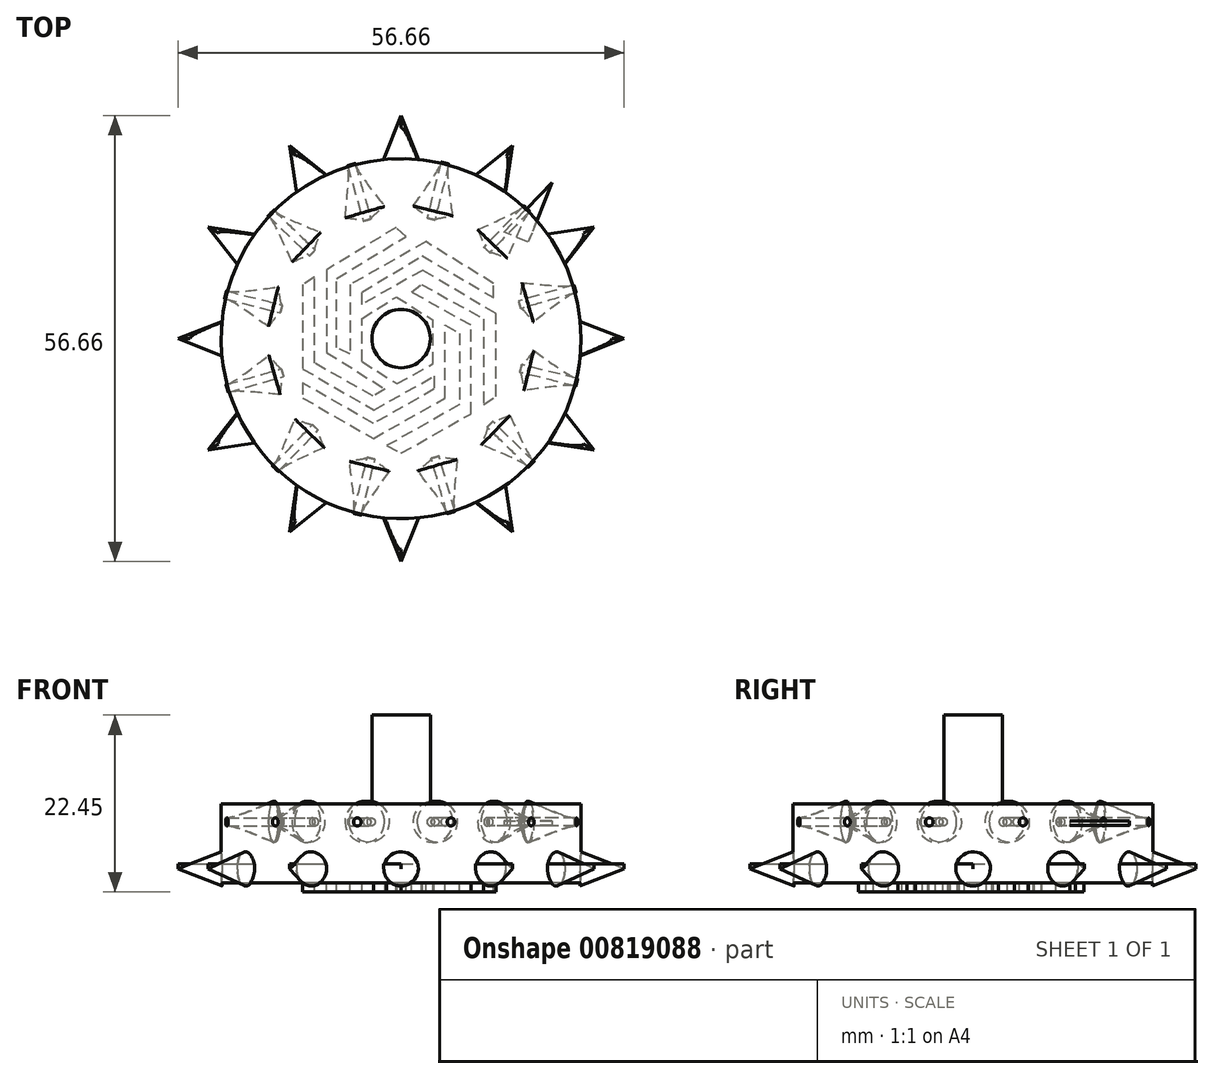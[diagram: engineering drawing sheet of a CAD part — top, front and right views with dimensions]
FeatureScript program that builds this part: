
annotation { "Feature Type Name" : "Feature", "Feature Type Description" : "" }
export const myFeature = defineFeature(function(context is Context, id is Id, definition is map)
    precondition{}
    {
        {
            var Q0;
            Q0=qCreatedBy(makeId("Top.planeOp"),FACE);
            var sketch = newSketch(context, id + "F0", { "sketchPlane" : qUnion([Q0])});
            skCircle(sketch, "E0", {"center": v(0, 0) * mm, "radius": 19.05 * mm});
            skSolve(sketch);
        }
        {
            var Q0;
            Q0=makeQuery(id+"F0.imprint","IMPRINT",FACE,{"disambiguationData":[TD([[makeQuery(id+"F0.imprint","IMPRINT",EDGE,{"derivedFrom":sQuery(id+"F0.wireOp",EDGE,"E0")}),1.0]])]});
            extrude(context, id + "F1", {"entities" : qUnion([Q0]), "depth" : 8.38 * mm, "offsetDistance" : 25.4 * mm});
        }
        {
            var Q0;
            Q0=makeQuery(id+"F1.opExtrude","CAP_FACE",FACE,{"disambiguationData":[OSD([sQuery(id+"F0.wireOp",EDGE,"E0")])],"isStart":false});
            var sketch = newSketch(context, id + "F2", { "sketchPlane" : qUnion([Q0])});
            skCircle(sketch, "E1", {"center": v(0, 0) * mm, "radius": 3.1 * mm});
            skSolve(sketch);
        }
        {
            var Q0;
            Q0=makeQuery(id+"F2.imprint","IMPRINT",FACE,{"disambiguationData":[TD([[makeQuery(id+"F2.imprint","IMPRINT",EDGE,{"derivedFrom":sQuery(id+"F2.wireOp",EDGE,"E1")}),1.0]])]});
            extrude(context, id + "F3", {"entities" : qUnion([Q0]), "operationType" : NewBodyOperationType.ADD, "depth" : 9.4 * mm, "offsetDistance" : 25.4 * mm});
        }
        {
            var Q0;
            Q0=qCreatedBy(makeId("Top.planeOp"),FACE);
            cPlane(context, id + "F4", {"entities" : qUnion([Q0]), "cplaneType" : CPlaneType.OFFSET, "offset" : 2.03 * mm, "width" : 152.4 * mm, "height" : 152.4 * mm});
        }
        {
            var Q0;
            Q0=qCreatedBy(id+"F4.planeOp",FACE);
            var sketch = newSketch(context, id + "F5", { "sketchPlane" : qUnion([Q0])});
            skLineSegment(sketch, "E2", {"start": v(0, 17.1) * mm, "end": v(0, 23.6) * mm});
            skLineSegment(sketch, "E3", {"start": v(0, 23.6) * mm, "end": v(2.57, 17.1) * mm});
            skLineSegment(sketch, "E4", {"start": v(0, 17.1) * mm, "end": v(2.57, 17.1) * mm});
            skSolve(sketch);
        }
        {
            var Q0;
            Q0=qSketchRegion(id+"F5",true);
            extrude(context, id + "F6", {"entities" : qUnion([Q0]), "operationType" : NewBodyOperationType.ADD, "oppositeDirection" : true, "depth" : 0.5 * mm, "offsetDistance" : 25.4 * mm});
        }
        {
            var Q0;
            Q0=makeQuery(id+"F6.opExtrude","CAP_FACE",FACE,{"disambiguationData":[OSD([sQuery(id+"F5.wireOp",EDGE,"E2"),sQuery(id+"F5.wireOp",EDGE,"E3"),sQuery(id+"F5.wireOp",EDGE,"E4")])],"isStart":false});
            var Q1;
            Q1=makeQuery(id+"F6.opExtrude","CAP_EDGE",EDGE,{"disambiguationData":[OSD([sQuery(id+"F5.wireOp",EDGE,"E2")])],"isStart":false});
            revolve(context, id + "F7", {"operationType" : NewBodyOperationType.ADD, "surfaceOperationType" : NewSurfaceOperationType.NEW, "entities" : qUnion([Q0]), "axis" : qUnion([Q1]), "revolveType" : RevolveType.FULL});
        }
        {
            var Q0;
            Q0=makeQuery(id+"F1.opExtrude","SWEPT_BODY",BODY,{"disambiguationData":[OSD([sQuery(id+"F0.wireOp",EDGE,"E0")])]});
            var Q1;
            Q1=makeQuery(id+"F3.opExtrude","CAP_EDGE",EDGE,{"disambiguationData":[OSD([sQuery(id+"F2.wireOp",EDGE,"E1")])],"isStart":false});
            circularPattern(context, id + "F8", {"entities" : qUnion([Q0]), "axis" : qUnion([Q1]), "angle" : 360 * degree, "instanceCount" : 12, "equalSpace" : true});
        }
        {
            var Q0;
            Q0=qCreatedBy(id+"F4.planeOp",FACE);
            cPlane(context, id + "F9", {"entities" : qUnion([Q0]), "cplaneType" : CPlaneType.OFFSET, "offset" : 4.06 * mm, "width" : 152.4 * mm, "height" : 152.4 * mm});
        }
        {
            var Q0;
            Q0=qCreatedBy(id+"F9.planeOp",FACE);
            var sketch = newSketch(context, id + "F10", { "sketchPlane" : qUnion([Q0])});
            skLineSegment(sketch, "E5", {"start": v(0, 0) * mm, "end": v(15.97, 16.54) * mm});
            skLineSegment(sketch, "E6", {"start": v(15.97, 16.54) * mm, "end": v(13.46, 10.25) * mm});
            skLineSegment(sketch, "E7", {"start": v(13.46, 10.25) * mm, "end": v(10.89, 11.27) * mm});
            skSolve(sketch);
        }
        {
            var Q0;
            Q0=qSketchRegion(id+"F10",true);
            extrude(context, id + "F11", {"entities" : qUnion([Q0]), "depth" : 0.5 * mm, "offsetDistance" : 25.4 * mm});
        }
        {
            var Q0;
            Q0=makeQuery(id+"F11.opExtrude","CAP_FACE",FACE,{"disambiguationData":[OSD([sQuery(id+"F10.wireOp",EDGE,"E5"),sQuery(id+"F10.wireOp",EDGE,"E6"),sQuery(id+"F10.wireOp",EDGE,"E7")])],"isStart":false});
            var Q1;
            Q1=makeQuery(id+"F11.opExtrude","CAP_EDGE",EDGE,{"disambiguationData":[OSD([sQuery(id+"F10.wireOp",EDGE,"E5")])],"isStart":true});
            revolve(context, id + "F12", {"surfaceOperationType" : NewSurfaceOperationType.NEW, "entities" : qUnion([Q0]), "axis" : qUnion([Q1]), "revolveType" : RevolveType.FULL});
        }
        {
            var Q0;
            Q0=makeQuery(id+"F12.opRevolve","SWEPT_BODY",BODY,{"disambiguationData":[OSD([sQuery(id+"F10.wireOp",EDGE,"E5"),sQuery(id+"F10.wireOp",EDGE,"E6"),sQuery(id+"F10.wireOp",EDGE,"E7")])]});
            var Q1;
            Q1=makeQuery(id+"F3.opExtrude","CAP_EDGE",EDGE,{"disambiguationData":[OSD([sQuery(id+"F2.wireOp",EDGE,"E1")])],"isStart":false});
            circularPattern(context, id + "F13", {"entities" : qUnion([Q0]), "axis" : qUnion([Q1]), "angle" : 360 * degree, "instanceCount" : 12, "equalSpace" : true});
        }
        {
            var Q0;
            Q0=makeQuery(id+"F8.opPattern","COPY",BODY,{"derivedFrom":makeQuery(id+"F1.opExtrude","SWEPT_BODY",BODY,{"disambiguationData":[OSD([sQuery(id+"F0.wireOp",EDGE,"E0")])]}),"instanceName":"6"});
            var Q1;
            Q1=makeQuery(id+"F8.opPattern","COPY",BODY,{"derivedFrom":makeQuery(id+"F1.opExtrude","SWEPT_BODY",BODY,{"disambiguationData":[OSD([sQuery(id+"F0.wireOp",EDGE,"E0")])]}),"instanceName":"5"});
            var Q2;
            Q2=makeQuery(id+"F8.opPattern","COPY",BODY,{"derivedFrom":makeQuery(id+"F1.opExtrude","SWEPT_BODY",BODY,{"disambiguationData":[OSD([sQuery(id+"F0.wireOp",EDGE,"E0")])]}),"instanceName":"3"});
            var Q3;
            Q3=makeQuery(id+"F1.opExtrude","SWEPT_BODY",BODY,{"disambiguationData":[OSD([sQuery(id+"F0.wireOp",EDGE,"E0")])]});
            var Q4;
            Q4=makeQuery(id+"F8.opPattern","COPY",BODY,{"derivedFrom":makeQuery(id+"F1.opExtrude","SWEPT_BODY",BODY,{"disambiguationData":[OSD([sQuery(id+"F0.wireOp",EDGE,"E0")])]}),"instanceName":"11"});
            var Q5;
            Q5=makeQuery(id+"F8.opPattern","COPY",BODY,{"derivedFrom":makeQuery(id+"F1.opExtrude","SWEPT_BODY",BODY,{"disambiguationData":[OSD([sQuery(id+"F0.wireOp",EDGE,"E0")])]}),"instanceName":"8"});
            var Q6;
            Q6=makeQuery(id+"F8.opPattern","COPY",BODY,{"derivedFrom":makeQuery(id+"F1.opExtrude","SWEPT_BODY",BODY,{"disambiguationData":[OSD([sQuery(id+"F0.wireOp",EDGE,"E0")])]}),"instanceName":"9"});
            var Q7;
            Q7=makeQuery(id+"F8.opPattern","COPY",BODY,{"derivedFrom":makeQuery(id+"F1.opExtrude","SWEPT_BODY",BODY,{"disambiguationData":[OSD([sQuery(id+"F0.wireOp",EDGE,"E0")])]}),"instanceName":"10"});
            var Q8;
            Q8=makeQuery(id+"F8.opPattern","COPY",BODY,{"derivedFrom":makeQuery(id+"F1.opExtrude","SWEPT_BODY",BODY,{"disambiguationData":[OSD([sQuery(id+"F0.wireOp",EDGE,"E0")])]}),"instanceName":"7"});
            var Q9;
            Q9=makeQuery(id+"F8.opPattern","COPY",BODY,{"derivedFrom":makeQuery(id+"F1.opExtrude","SWEPT_BODY",BODY,{"disambiguationData":[OSD([sQuery(id+"F0.wireOp",EDGE,"E0")])]}),"instanceName":"4"});
            var Q10;
            Q10=makeQuery(id+"F8.opPattern","COPY",BODY,{"derivedFrom":makeQuery(id+"F1.opExtrude","SWEPT_BODY",BODY,{"disambiguationData":[OSD([sQuery(id+"F0.wireOp",EDGE,"E0")])]}),"instanceName":"2"});
            var Q11;
            Q11=makeQuery(id+"F11.opExtrude","SWEPT_BODY",BODY,{"disambiguationData":[OSD([sQuery(id+"F10.wireOp",EDGE,"E5"),sQuery(id+"F10.wireOp",EDGE,"E6"),sQuery(id+"F10.wireOp",EDGE,"E7")])]});
            var Q12;
            Q12=makeQuery(id+"F8.opPattern","COPY",BODY,{"derivedFrom":makeQuery(id+"F1.opExtrude","SWEPT_BODY",BODY,{"disambiguationData":[OSD([sQuery(id+"F0.wireOp",EDGE,"E0")])]}),"instanceName":"1"});
            var Q13;
            Q13=sQuery(id+"F2.wireOp",VERTEX,"E1.center");
            transform(context, id + "F14", {"entities" : qUnion([Q0, Q1, Q2, Q3, Q4, Q5, Q6, Q7, Q8, Q9, Q10, Q11, Q12]), "transformType" : TransformType.SCALE_UNIFORMLY, "scale" : 1.2, "scalePoint" : qUnion([Q13]), "makeCopy" : false});
        }
        {
            var Q0;
            Q0=qCreatedBy(makeId("Top.planeOp"),FACE);
            var sketch = newSketch(context, id + "F15", { "sketchPlane" : qUnion([Q0])});
            skLineSegment(sketch, "E8", {"start": v(-12.5, 6.89) * mm, "end": v(-12.5, -3.83) * mm});
            skLineSegment(sketch, "E9", {"start": v(-12.5, -3.83) * mm, "end": v(-3.44, -9.07) * mm});
            skLineSegment(sketch, "E10", {"start": v(-3.44, -9.07) * mm, "end": v(4.2, -4.76) * mm});
            skLineSegment(sketch, "E11", {"start": v(4.2, -4.76) * mm, "end": v(4.2, -6.42) * mm});
            skLineSegment(sketch, "E12", {"start": v(4.2, -6.42) * mm, "end": v(-3.52, -10.78) * mm});
            skLineSegment(sketch, "E13", {"start": v(-3.52, -10.78) * mm, "end": v(-12.5, -5.62) * mm});
            skLineSegment(sketch, "E14", {"start": v(-12.5, -5.62) * mm, "end": v(-12.5, -7.53) * mm});
            skLineSegment(sketch, "E15", {"start": v(-12.5, -7.53) * mm, "end": v(-3.52, -12.69) * mm});
            skLineSegment(sketch, "E16", {"start": v(-3.52, -12.69) * mm, "end": v(5.6, -7.54) * mm});
            skLineSegment(sketch, "E17", {"start": v(5.6, -7.54) * mm, "end": v(5.6, 1.71) * mm});
            skLineSegment(sketch, "E18", {"start": v(5.6, 1.71) * mm, "end": v(7.4, 0.68) * mm});
            skLineSegment(sketch, "E19", {"start": v(7.4, 0.68) * mm, "end": v(7.4, -8.4) * mm});
            skLineSegment(sketch, "E20", {"start": v(7.4, -8.4) * mm, "end": v(-1.82, -13.6) * mm});
            skLineSegment(sketch, "E21", {"start": v(-1.82, -13.6) * mm, "end": v(0, -14.55) * mm});
            skLineSegment(sketch, "E22", {"start": v(0, -14.55) * mm, "end": v(8.86, -9.55) * mm});
            skLineSegment(sketch, "E23", {"start": v(8.86, -9.55) * mm, "end": v(8.86, 1.71) * mm});
            skLineSegment(sketch, "E24", {"start": v(8.86, 1.71) * mm, "end": v(1.3, 5.9) * mm});
            skLineSegment(sketch, "E25", {"start": v(1.3, 5.9) * mm, "end": v(2.6, 6.89) * mm});
            skLineSegment(sketch, "E26", {"start": v(2.6, 6.89) * mm, "end": v(10.49, 2.51) * mm});
            skLineSegment(sketch, "E27", {"start": v(10.49, 2.51) * mm, "end": v(10.49, -8.4) * mm});
            skLineSegment(sketch, "E28", {"start": v(10.49, -8.4) * mm, "end": v(12.03, -7.34) * mm});
            skLineSegment(sketch, "E29", {"start": v(12.03, -7.34) * mm, "end": v(12.03, 3.2) * mm});
            skLineSegment(sketch, "E30", {"start": v(12.03, 3.2) * mm, "end": v(2.72, 8.68) * mm});
            skLineSegment(sketch, "E31", {"start": v(2.72, 8.68) * mm, "end": v(-4.98, 4.36) * mm});
            skLineSegment(sketch, "E32", {"start": v(-4.98, 4.36) * mm, "end": v(-4.98, 5.9) * mm});
            skLineSegment(sketch, "E33", {"start": v(-4.98, 5.9) * mm, "end": v(2.66, 10.52) * mm});
            skLineSegment(sketch, "E34", {"start": v(2.66, 10.52) * mm, "end": v(11.72, 5.23) * mm});
            skLineSegment(sketch, "E35", {"start": v(11.72, 5.23) * mm, "end": v(11.72, 7.01) * mm});
            skLineSegment(sketch, "E36", {"start": v(11.72, 7.01) * mm, "end": v(3.15, 12.31) * mm});
            skLineSegment(sketch, "E37", {"start": v(3.15, 12.31) * mm, "end": v(-6.46, 6.89) * mm});
            skLineSegment(sketch, "E38", {"start": v(-6.46, 6.89) * mm, "end": v(-6.46, -1.98) * mm});
            skLineSegment(sketch, "E39", {"start": v(-6.46, -1.98) * mm, "end": v(-8.18, -1.12) * mm});
            skLineSegment(sketch, "E40", {"start": v(-8.18, -1.12) * mm, "end": v(-8.18, 7.63) * mm});
            skLineSegment(sketch, "E41", {"start": v(-8.18, 7.63) * mm, "end": v(0.63, 12.99) * mm});
            skLineSegment(sketch, "E42", {"start": v(0.63, 12.99) * mm, "end": v(-0.67, 14.1) * mm});
            skLineSegment(sketch, "E43", {"start": v(-0.67, 14.1) * mm, "end": v(-9.48, 8.74) * mm});
            skLineSegment(sketch, "E44", {"start": v(-9.48, 8.74) * mm, "end": v(-9.48, -1.74) * mm});
            skLineSegment(sketch, "E45", {"start": v(-9.48, -1.74) * mm, "end": v(-2.02, -6.42) * mm});
            skLineSegment(sketch, "E46", {"start": v(-2.02, -6.42) * mm, "end": v(-3.56, -7.28) * mm});
            skLineSegment(sketch, "E47", {"start": v(-3.56, -7.28) * mm, "end": v(-11.02, -3.1) * mm});
            skLineSegment(sketch, "E48", {"start": v(-11.02, -3.1) * mm, "end": v(-11.02, 7.81) * mm});
            skLineSegment(sketch, "E49", {"start": v(-11.02, 7.81) * mm, "end": v(-12.5, 6.89) * mm});
            skLineSegment(sketch, "E50", {"start": v(-4.98, -2.9) * mm, "end": v(-0.48, -5.73) * mm});
            skLineSegment(sketch, "E51", {"start": v(-0.48, -5.73) * mm, "end": v(4.04, -3.18) * mm});
            skLineSegment(sketch, "E52", {"start": v(4.04, -3.18) * mm, "end": v(4.04, 2.4) * mm});
            skLineSegment(sketch, "E53", {"start": v(-4.98, -2.9) * mm, "end": v(-4.98, 2.58) * mm});
            skLineSegment(sketch, "E54", {"start": v(-4.98, 2.58) * mm, "end": v(-0.6, 5.29) * mm});
            skLineSegment(sketch, "E55", {"start": v(-0.6, 5.29) * mm, "end": v(4.04, 2.4) * mm});
            skSolve(sketch);
        }
        {
            var Q0;
            Q0 = qSketchRegion(id + "F15", true);
            extrude(context, id + "F16", {"entities" : qUnion([Q0]), "operationType" : NewBodyOperationType.ADD, "oppositeDirection" : true, "depth" : 2.8 * mm, "offsetDistance" : 25.4 * mm});
        }
    });
